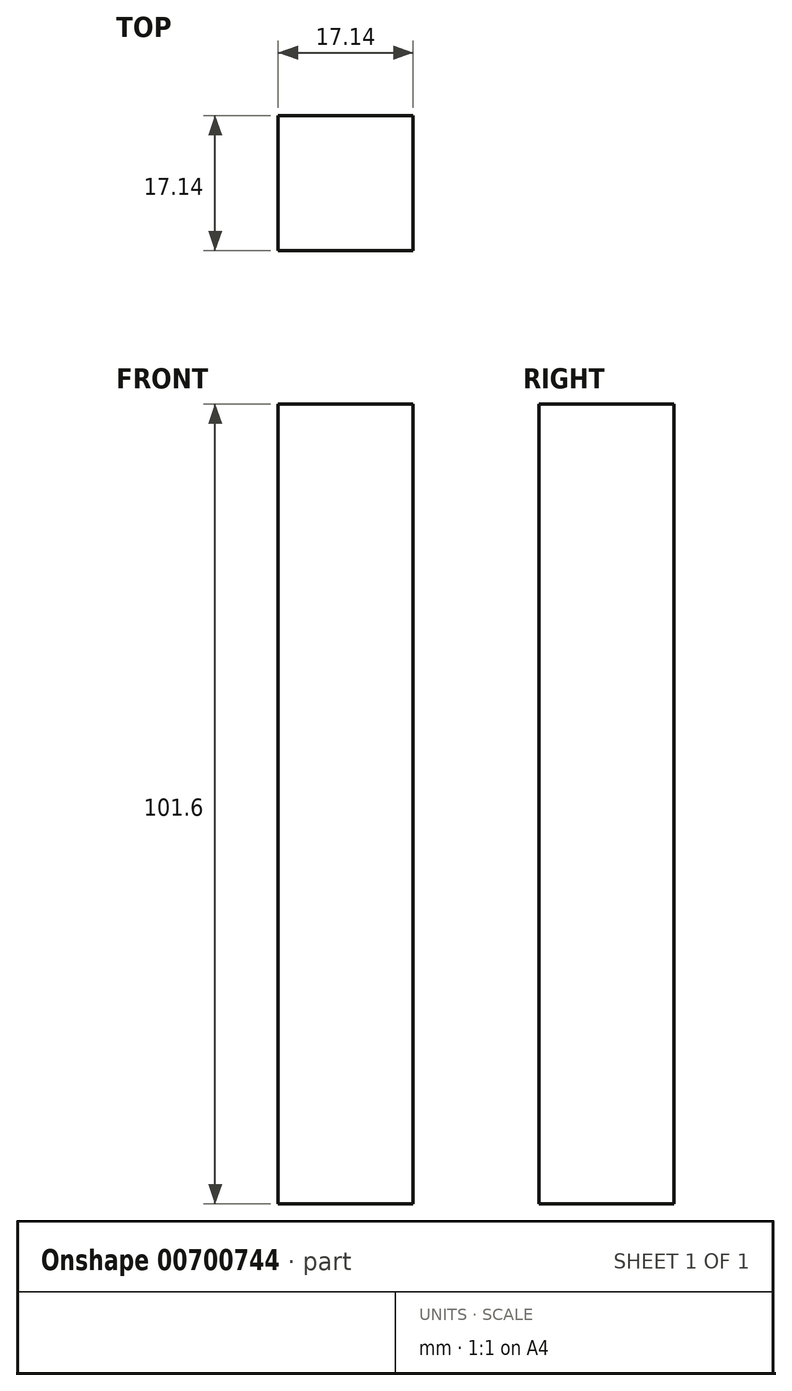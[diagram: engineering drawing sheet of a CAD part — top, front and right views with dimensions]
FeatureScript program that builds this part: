
annotation { "Feature Type Name" : "Feature", "Feature Type Description" : "" }
export const myFeature = defineFeature(function(context is Context, id is Id, definition is map)
    precondition{}
    {
        {
            var Q0;
            Q0=qCreatedBy(makeId("Front.planeOp"),FACE);
            var sketch = newSketch(context, id + "F0", { "sketchPlane" : qUnion([Q0])});
            skLineSegment(sketch, "E0.bottom", {"start": v(0, 0) * mm, "end": v(17.15, 0) * mm});
            skLineSegment(sketch, "E0.top", {"start": v(0, 101.6) * mm, "end": v(17.14, 101.6) * mm});
            skLineSegment(sketch, "E0.left", {"start": v(0, 0) * mm, "end": v(0, 101.6) * mm});
            skLineSegment(sketch, "E0.right", {"start": v(17.15, 0) * mm, "end": v(17.14, 101.6) * mm});
            skSolve(sketch);
        }
        {
            var Q0;
            Q0 = qSketchRegion(id + "F0", true);
            extrude(context, id + "F1", {"entities" : qUnion([Q0]), "depth" : 17.14 * mm, "offsetDistance" : 25.4 * mm});
        }
    });
